FCSTD DOCUMENT  (FreeCAD 0.15R4671 (Git))
Label: BottomCorner
License: All rights reserved
LicenseURL: http://en.wikipedia.org/wiki/All_rights_reserved
objects: Sketcher::SketchObject×16, PartDesign::Pocket×15, Part::Feature×6, PartDesign::Fillet×4, Mesh::Feature×3, PartDesign::Chamfer×2, PartDesign::Pad×1
note: 60 computed .brp shape members not serialized (recipe doc carries the construction recipe); baked Part::Feature solids carry a one-line shape summary decoded from their .brp

FEATURE [Mesh::Feature] tempTopCornerCap
FEATURE [Part::Feature] Part__Feature  label="OB1515_45mm001"
  Placement = pos=(0,-20.5,15.5) rot=(1,0,0;1.5708rad)
  shape: bbox 15 x 45 x 15 mm, 158 faces (baked)
FEATURE [Part::Feature] Part__Feature001  label="OB1515_45mm002"
  Placement = pos=(20.5,0,15.5) rot=(0.57735,0.57735,0.57735;2.0944rad)
  shape: bbox 45 x 15 x 15 mm, 158 faces (baked)
FEATURE [Part::Feature] Part__Feature002  label="OB1515_45mm"
  Placement = pos=(7,-7,1) rot=(0,0,1;0.785398rad)
  shape: bbox 21.01 x 21.01 x 45 mm, 158 faces (baked)
FEATURE [Sketcher::SketchObject] Sketch
  Placement = pos=(0,0,8) rot=(0,0,1;0rad)
  sketch-geometry (9):
    g0: LineSegment StartX=-7.5 StartY=7.5 StartZ=0 EndX=65.5 EndY=7.5 EndZ=0
    g1: LineSegment StartX=65.5 StartY=7.5 StartZ=0 EndX=65.5 EndY=-14.5 EndZ=0
    g2: LineSegment StartX=65.5 StartY=-14.5 StartZ=0 EndX=14.5 EndY=-65.5 EndZ=0
    g3: LineSegment StartX=14.5 StartY=-65.5 StartZ=0 EndX=-7.5 EndY=-65.5 EndZ=0
    g4: LineSegment StartX=-7.5 StartY=-65.5 StartZ=0 EndX=-7.5 EndY=7.5 EndZ=0
    g5: LineSegment StartX=7 StartY=4 StartZ=0 EndX=18 EndY=-7 EndZ=0
    g6: LineSegment StartX=18 StartY=-7 StartZ=0 EndX=7 EndY=-18 EndZ=0
    g7: LineSegment StartX=7 StartY=-18 StartZ=0 EndX=-4 EndY=-7 EndZ=0
    g8: LineSegment StartX=-4 StartY=-7 StartZ=0 EndX=7 EndY=4 EndZ=0
  constraints (18):
    c: Coincident(g0,g1)
    c: Coincident(g1,g2)
    c: Coincident(g2,g3)
    c: Coincident(g3,g4)
    c: Coincident(g4,g0)
    c: Horizontal(g3)
    c: Horizontal(g0)
    c: Vertical(g1)
    c: Vertical(g4)
    c: Angle(g2,g-2) = 0.785398
    c: DistanceX(g0) = -7.5
    c: DistanceY(g0) = 7.5
    c: Coincident(g5,g6)
    c: Coincident(g6,g7)
    c: Coincident(g7,g8)
    c: Coincident(g8,g5)
    c: DistanceY(g3) = -65.5
    c: DistanceX(g0) = 65.5
FEATURE [PartDesign::Pad] Pad
  Length = 88
  Length2 = 100
  Placement = pos=(0,0,8) rot=(0,0,1;0rad)
  Sketch = -> Sketch
  Type = 0
FEATURE [Part::Feature] Part__Feature003  label="OB1515_45mm003"
  Placement = pos=(0,-20.5,88.5) rot=(1,0,0;1.5708rad)
  shape: bbox 15 x 45 x 15 mm, 158 faces (baked)
FEATURE [Part::Feature] Part__Feature004  label="OB1515_45mm004"
  Placement = pos=(20.5,0,88.5) rot=(0.57735,0.57735,0.57735;2.0944rad)
  shape: bbox 45 x 15 x 15 mm, 158 faces (baked)
FEATURE [Sketcher::SketchObject] Sketch001
  Placement = pos=(0,0,96) rot=(0,0,1;0rad)
  Support = -> Pad [Face11]
  sketch-geometry (8):
    g0: LineSegment StartX=20.5 StartY=8.5 StartZ=0 EndX=66.5 EndY=8.5 EndZ=0
    g1: LineSegment StartX=66.5 StartY=8.5 StartZ=0 EndX=66.5 EndY=-7.5 EndZ=0
    g2: LineSegment StartX=66.5 StartY=-7.5 StartZ=0 EndX=20.5 EndY=-7.5 EndZ=0
    g3: LineSegment StartX=20.5 StartY=-7.5 StartZ=0 EndX=20.5 EndY=8.5 EndZ=0
    g4: LineSegment StartX=-8.5 StartY=-20.5 StartZ=0 EndX=7.5 EndY=-20.5 EndZ=0
    g5: LineSegment StartX=7.5 StartY=-20.5 StartZ=0 EndX=7.5 EndY=-66 EndZ=0
    g6: LineSegment StartX=7.5 StartY=-66 StartZ=0 EndX=-8.5 EndY=-66 EndZ=0
    g7: LineSegment StartX=-8.5 StartY=-66 StartZ=0 EndX=-8.5 EndY=-20.5 EndZ=0
  constraints (16):
    c: Coincident(g0,g1)
    c: Coincident(g1,g2)
    c: Coincident(g2,g3)
    c: Coincident(g3,g0)
    c: Horizontal(g0)
    c: Horizontal(g2)
    c: Vertical(g1)
    c: Vertical(g3)
    c: Coincident(g4,g5)
    c: Coincident(g5,g6)
    c: Coincident(g6,g7)
    c: Coincident(g7,g4)
    c: Horizontal(g4)
    c: Horizontal(g6)
    c: Vertical(g5)
    c: Vertical(g7)
FEATURE [PartDesign::Pocket] Pocket
  Length = 5
  Placement = pos=(0,0,8) rot=(0,0,1;0rad)
  Sketch = -> Sketch001
  Type = 1
FEATURE [Sketcher::SketchObject] Sketch002
  Placement = pos=(0,0,96) rot=(0,0,1;0rad)
  Support = -> Pocket [Face4]
  sketch-geometry (4):
    g0: LineSegment StartX=66.5 StartY=-14.5 StartZ=0 EndX=20.5 EndY=-14.5 EndZ=0
    g1: LineSegment StartX=20.5 StartY=-14.5 StartZ=0 EndX=14.5 EndY=-20.5 EndZ=0
    g2: LineSegment StartX=14.5 StartY=-20.5 StartZ=0 EndX=14.5 EndY=-66.5 EndZ=0
    g3: LineSegment StartX=14.5 StartY=-66.5 StartZ=0 EndX=66.5 EndY=-14.5 EndZ=0
  constraints (4):
    c: Coincident(g0,g1)
    c: Coincident(g1,g2)
    c: Coincident(g2,g3)
    c: Coincident(g3,g0)
FEATURE [PartDesign::Pocket] Pocket001
  Length = 81
  Placement = pos=(0,0,8) rot=(0,0,1;0rad)
  Sketch = -> Sketch002
  Type = 0
FEATURE [Sketcher::SketchObject] Sketch003
  Placement = pos=(17.5,-17.5,8) rot=(0.862856,0.357407,0.357407;1.71777rad)
  Support = -> Pocket001 [Face17]
  sketch-geometry (4):
    g0: ArcOfCircle CenterX=0 CenterY=12 CenterZ=0 NormalX=0 NormalY=0 NormalZ=1 Radius=1.52224 StartAngle=3.14159 EndAngle=6.28319
    g1: ArcOfCircle CenterX=0 CenterY=83 CenterZ=0 NormalX=0 NormalY=0 NormalZ=1 Radius=1.52224 StartAngle=0 EndAngle=3.14159
    g2: LineSegment StartX=1.52224 StartY=12 StartZ=0 EndX=1.52224 EndY=83 EndZ=0
    g3: LineSegment StartX=-1.52224 StartY=12 StartZ=0 EndX=-1.52224 EndY=83 EndZ=0
  constraints (6):
    c: Tangent(g0,g3) = 1.5708
    c: Tangent(g0,g2) = -1.5708
    c: Tangent(g2,g1) = -1.5708
    c: Tangent(g3,g1) = 1.5708
    c: Vertical(g2)
    c: Equal(g0,g1)
FEATURE [PartDesign::Pocket] Pocket002
  Length = 15
  Placement = pos=(0,0,8) rot=(0,0,1;0rad)
  Sketch = -> Sketch003
  Type = 0
FEATURE [PartDesign::Chamfer] Chamfer
  Base = -> Pocket002 [Edge4]
  Placement = pos=(0,0,8) rot=(0,0,1;0rad)
  Size = 8
FEATURE [PartDesign::Fillet] Fillet
  Base = -> Chamfer [Edge2,Edge18]
  Placement = pos=(0,0,8) rot=(0,0,1;0rad)
  Radius = 4
FEATURE [Sketcher::SketchObject] Sketch004
  Placement = pos=(0,0,15) rot=(0,0,1;0rad)
  Support = -> Fillet [Face22]
  sketch-geometry (1):
    g0: Circle CenterX=30 CenterY=-30 CenterZ=0 NormalX=0 NormalY=0 NormalZ=1 Radius=2.75
  constraints (1):
    c: Radius(g0) = 2.75
FEATURE [PartDesign::Pocket] Pocket003
  Length = 5
  Placement = pos=(0,0,8) rot=(0,0,1;0rad)
  Sketch = -> Sketch004
  Type = 1
FEATURE [Sketcher::SketchObject] Sketch005
  Placement = pos=(0,-14.5,8) rot=(1,0,0;1.5708rad)
  Support = -> Pocket003 [Face20]
  sketch-geometry (4):
    g0: Circle CenterX=60 CenterY=7.5 CenterZ=0 NormalX=0 NormalY=0 NormalZ=1 Radius=1.8
    g1: Circle CenterX=25 CenterY=7.5 CenterZ=0 NormalX=0 NormalY=0 NormalZ=1 Radius=1.8
    g2: Circle CenterX=25 CenterY=80.5 CenterZ=0 NormalX=0 NormalY=0 NormalZ=1 Radius=1.8
    g3: Circle CenterX=60 CenterY=80.5 CenterZ=0 NormalX=0 NormalY=0 NormalZ=1 Radius=1.8
  constraints (4):
    c: Radius(g2) = 1.8
    c: Radius(g3) = 1.8
    c: Radius(g0) = 1.8
    c: Radius(g1) = 1.8
FEATURE [PartDesign::Pocket] Pocket004
  Length = 5
  Placement = pos=(0,0,8) rot=(0,0,1;0rad)
  Sketch = -> Sketch005
  Type = 1
FEATURE [Sketcher::SketchObject] Sketch006
  Placement = pos=(14.5,0,8) rot=(0.57735,0.57735,0.57735;2.0944rad)
  Support = -> Pocket004 [Face22]
  sketch-geometry (4):
    g0: Circle CenterX=-60 CenterY=7.5 CenterZ=0 NormalX=0 NormalY=0 NormalZ=1 Radius=1.8
    g1: Circle CenterX=-25 CenterY=7.5 CenterZ=0 NormalX=0 NormalY=0 NormalZ=1 Radius=1.8
    g2: Circle CenterX=-60 CenterY=80.5 CenterZ=0 NormalX=0 NormalY=0 NormalZ=1 Radius=1.8
    g3: Circle CenterX=-25 CenterY=80.5 CenterZ=0 NormalX=0 NormalY=0 NormalZ=1 Radius=1.8
  constraints (4):
    c: Radius(g2) = 1.8
    c: Radius(g3) = 1.8
    c: Radius(g1) = 1.8
    c: Radius(g0) = 1.8
FEATURE [PartDesign::Pocket] Pocket005
  Length = 5
  Placement = pos=(0,0,8) rot=(0,0,1;0rad)
  Sketch = -> Sketch006
  Type = 1
FEATURE [PartDesign::Fillet] Fillet001
  Base = -> Pocket005 [Edge80,Edge69]
  Placement = pos=(0,0,8) rot=(0,0,1;0rad)
  Radius = 4
FEATURE [Sketcher::SketchObject] Sketch007
  Placement = pos=(14.5,0,8) rot=(0.57735,0.57735,0.57735;2.0944rad)
  Support = -> Fillet001 [Face9]
  sketch-geometry (4):
    g0: Circle CenterX=-60 CenterY=80.5 CenterZ=0 NormalX=0 NormalY=0 NormalZ=1 Radius=3.6
    g1: Circle CenterX=-25 CenterY=80.5 CenterZ=0 NormalX=0 NormalY=0 NormalZ=1 Radius=3.6
    g2: Circle CenterX=-60 CenterY=7.5 CenterZ=0 NormalX=0 NormalY=0 NormalZ=1 Radius=3.6
    g3: Circle CenterX=-25 CenterY=7.5 CenterZ=0 NormalX=0 NormalY=0 NormalZ=1 Radius=3.6
  constraints (4):
    c: Radius(g0) = 3.6
    c: Radius(g1) = 3.6
    c: Radius(g2) = 3.6
    c: Radius(g3) = 3.6
FEATURE [PartDesign::Pocket] Pocket006
  Length = 6
  Midplane = true
  Placement = pos=(0,0,8) rot=(0,0,1;0rad)
  Sketch = -> Sketch007
  Type = 0
FEATURE [Sketcher::SketchObject] Sketch008
  Placement = pos=(0,-14.5,8) rot=(1,0,0;1.5708rad)
  Support = -> Pocket006 [Face2]
  sketch-geometry (4):
    g0: Circle CenterX=60 CenterY=7.5 CenterZ=0 NormalX=0 NormalY=0 NormalZ=1 Radius=3.6
    g1: Circle CenterX=25 CenterY=7.5 CenterZ=0 NormalX=0 NormalY=0 NormalZ=1 Radius=3.6
    g2: Circle CenterX=25 CenterY=80.5 CenterZ=0 NormalX=0 NormalY=0 NormalZ=1 Radius=3.6
    g3: Circle CenterX=60 CenterY=80.5 CenterZ=0 NormalX=0 NormalY=0 NormalZ=1 Radius=3.6
  constraints (4):
    c: Radius(g2) = 3.6
    c: Radius(g3) = 3.6
    c: Radius(g1) = 3.6
    c: Radius(g0) = 3.6
FEATURE [PartDesign::Pocket] Pocket007
  Length = 6
  Midplane = true
  Placement = pos=(0,0,8) rot=(0,0,1;0rad)
  Sketch = -> Sketch008
  Type = 0
FEATURE [Sketcher::SketchObject] Sketch009
  Placement = pos=(0,0,15) rot=(0,0,1;0rad)
  Support = -> Pocket007 [Face24]
  sketch-geometry (8):
    g0: LineSegment StartX=56 StartY=-14.5 StartZ=0 EndX=65.5 EndY=-14.5 EndZ=0
    g1: LineSegment StartX=65.5 StartY=-14.5 StartZ=0 EndX=65.5 EndY=-24.5 EndZ=0
    g2: LineSegment StartX=65.5 StartY=-24.5 StartZ=0 EndX=56 EndY=-24.5 EndZ=0
    g3: LineSegment StartX=56 StartY=-24.5 StartZ=0 EndX=56 EndY=-14.5 EndZ=0
    g4: LineSegment StartX=14.5 StartY=-56 StartZ=0 EndX=29.7351 EndY=-56 EndZ=0
    g5: LineSegment StartX=29.7351 StartY=-56 StartZ=0 EndX=29.7351 EndY=-66 EndZ=0
    g6: LineSegment StartX=29.7351 StartY=-66 StartZ=0 EndX=14.5 EndY=-66 EndZ=0
    g7: LineSegment StartX=14.5 StartY=-66 StartZ=0 EndX=14.5 EndY=-56 EndZ=0
  constraints (16):
    c: Coincident(g0,g1)
    c: Coincident(g1,g2)
    c: Coincident(g2,g3)
    c: Coincident(g3,g0)
    c: Horizontal(g0)
    c: Horizontal(g2)
    c: Vertical(g1)
    c: Vertical(g3)
    c: Coincident(g4,g5)
    c: Coincident(g5,g6)
    c: Coincident(g6,g7)
    c: Coincident(g7,g4)
    c: Horizontal(g4)
    c: Horizontal(g6)
    c: Vertical(g5)
    c: Vertical(g7)
FEATURE [PartDesign::Pocket] Pocket008
  Length = 5
  Placement = pos=(0,0,8) rot=(0,0,1;0rad)
  Sketch = -> Sketch009
  Type = 1
FEATURE [PartDesign::Fillet] Fillet002
  Base = -> Pocket008 [Edge165,Edge164]
  Placement = pos=(0,0,8) rot=(0,0,1;0rad)
  Radius = 4
FEATURE [Sketcher::SketchObject] Sketch010
  Placement = pos=(0,-65.5,8) rot=(1,0,0;1.5708rad)
  Support = -> Fillet002 [Face20]
  sketch-geometry (6):
    g0: LineSegment StartX=15.5 StartY=73 StartZ=0 EndX=14.5 EndY=73 EndZ=0
    g1: LineSegment StartX=14.5 StartY=73 StartZ=0 EndX=11 EndY=69.5 EndZ=0
    g2: LineSegment StartX=11 StartY=69.5 StartZ=0 EndX=11 EndY=18.5 EndZ=0
    g3: LineSegment StartX=11 StartY=18.5 StartZ=0 EndX=14.5 EndY=15 EndZ=0
    g4: LineSegment StartX=14.5 StartY=15 StartZ=0 EndX=15.5 EndY=15 EndZ=0
    g5: LineSegment StartX=15.5 StartY=15 StartZ=0 EndX=15.5 EndY=73 EndZ=0
  constraints (6):
    c: Coincident(g0,g1)
    c: Coincident(g1,g2)
    c: Coincident(g2,g3)
    c: Coincident(g3,g4)
    c: Coincident(g4,g5)
    c: Coincident(g5,g0)
FEATURE [PartDesign::Pocket] Pocket009
  Length = 38
  Placement = pos=(0,0,8) rot=(0,0,1;0rad)
  Sketch = -> Sketch010
  Type = 0
FEATURE [Sketcher::SketchObject] Sketch011
  Placement = pos=(65.5,0,8) rot=(0.57735,0.57735,0.57735;2.0944rad)
  Support = -> Pocket009 [Face30]
  sketch-geometry (6):
    g0: LineSegment StartX=-15.5 StartY=73 StartZ=0 EndX=-14.5 EndY=73 EndZ=0
    g1: LineSegment StartX=-14.5 StartY=73 StartZ=0 EndX=-11 EndY=69.5 EndZ=0
    g2: LineSegment StartX=-11 StartY=69.5 StartZ=0 EndX=-11 EndY=18.5 EndZ=0
    g3: LineSegment StartX=-11 StartY=18.5 StartZ=0 EndX=-14.5 EndY=15 EndZ=0
    g4: LineSegment StartX=-14.5 StartY=15 StartZ=0 EndX=-15.5 EndY=15 EndZ=0
    g5: LineSegment StartX=-15.5 StartY=15 StartZ=0 EndX=-15.5 EndY=73 EndZ=0
  constraints (6):
    c: Coincident(g0,g1)
    c: Coincident(g1,g2)
    c: Coincident(g2,g3)
    c: Coincident(g3,g4)
    c: Coincident(g4,g5)
    c: Coincident(g5,g0)
FEATURE [PartDesign::Pocket] Pocket010
  Length = 38
  Placement = pos=(0,0,8) rot=(0,0,1;0rad)
  Sketch = -> Sketch011
  Type = 0
FEATURE [PartDesign::Chamfer] Chamfer001
  Base = -> Pocket010 [Edge26,Edge62]
  Placement = pos=(0,0,8) rot=(0,0,1;0rad)
  Size = 3.499
FEATURE [Sketcher::SketchObject] Sketch012
  Placement = pos=(-3.5,3.5,8) rot=(-0.281085,0.678598,0.678598;3.68962rad)
  Support = -> Chamfer001 [Face26]
  sketch-geometry (2):
    g0: Circle CenterX=0 CenterY=7.5 CenterZ=0 NormalX=0 NormalY=0 NormalZ=1 Radius=1.8
    g1: Circle CenterX=0 CenterY=80.5 CenterZ=0 NormalX=0 NormalY=0 NormalZ=1 Radius=1.8
  constraints (2):
    c: Radius(g1) = 1.8
    c: Radius(g0) = 1.8
FEATURE [PartDesign::Pocket] Pocket011
  Length = 15
  Placement = pos=(0,0,8) rot=(0,0,1;0rad)
  Sketch = -> Sketch012
  Type = 0
FEATURE [Sketcher::SketchObject] Sketch013
  Placement = pos=(-3.5,3.5,8) rot=(-0.281085,0.678598,0.678598;3.68962rad)
  Support = -> Pocket011 [Face26]
  sketch-geometry (2):
    g0: Circle CenterX=0 CenterY=80.5 CenterZ=0 NormalX=0 NormalY=0 NormalZ=1 Radius=3.6
    g1: Circle CenterX=0 CenterY=7.5 CenterZ=0 NormalX=0 NormalY=0 NormalZ=1 Radius=3.6
  constraints (2):
    c: Radius(g1) = 3.6
    c: Radius(g0) = 3.6
FEATURE [PartDesign::Pocket] Pocket012
  Length = 3
  Placement = pos=(0,0,8) rot=(0,0,1;0rad)
  Sketch = -> Sketch013
  Type = 0
FEATURE [Mesh::Feature] GEMINI_R  label="GEMINI R5"
FEATURE [Part::Feature] Pocket013  label="BottomCorner_1"
  shape: bbox 73 x 73 x 88 mm, 75 faces (baked)
FEATURE [Sketcher::SketchObject] Sketch014
  Placement = pos=(0,-65.5,0) rot=(1,0,0;1.5708rad)
  Support = -> Pocket013 [Face13]
  sketch-geometry (4):
    g0: LineSegment StartX=-10.5 StartY=98 StartZ=0 EndX=66.5 EndY=98 EndZ=0
    g1: LineSegment StartX=66.5 StartY=98 StartZ=0 EndX=66.5 EndY=23 EndZ=0
    g2: LineSegment StartX=66.5 StartY=23 StartZ=0 EndX=-10.5 EndY=23 EndZ=0
    g3: LineSegment StartX=-10.5 StartY=23 StartZ=0 EndX=-10.5 EndY=98 EndZ=0
  constraints (8):
    c: Coincident(g0,g1)
    c: Coincident(g1,g2)
    c: Coincident(g2,g3)
    c: Coincident(g3,g0)
    c: Horizontal(g0)
    c: Horizontal(g2)
    c: Vertical(g1)
    c: Vertical(g3)
FEATURE [PartDesign::Pocket] Pocket014  label="BottomShortCorner_1"
  Length = 5
  Sketch = -> Sketch014
  Type = 1
FEATURE [PartDesign::Fillet] Fillet003  label="BottomShortCorner"
  Base = -> Pocket014 [Edge28,Edge34]
  Radius = 2
FEATURE [Mesh::Feature] TopCornerIdler_II
FEATURE [Sketcher::SketchObject] Sketch015
  Placement = pos=(0,0,96) rot=(0,0,1;0rad)
  Support = -> Pocket013 [Face15]
  sketch-geometry (8):
    g0: LineSegment StartX=-0.75 StartY=-20 StartZ=0 EndX=0.75 EndY=-20 EndZ=0
    g1: LineSegment StartX=0.75 StartY=-20 StartZ=0 EndX=0.75 EndY=-21.25 EndZ=0
    g2: LineSegment StartX=0.75 StartY=-21.25 StartZ=0 EndX=-0.75 EndY=-21.25 EndZ=0
    g3: LineSegment StartX=-0.75 StartY=-21.25 StartZ=0 EndX=-0.75 EndY=-20 EndZ=0
    g4: LineSegment StartX=20 StartY=0.75 StartZ=0 EndX=23 EndY=0.75 EndZ=0
    g5: LineSegment StartX=23 StartY=0.75 StartZ=0 EndX=23 EndY=-0.75 EndZ=0
    g6: LineSegment StartX=23 StartY=-0.75 StartZ=0 EndX=20 EndY=-0.75 EndZ=0
    g7: LineSegment StartX=20 StartY=-0.75 StartZ=0 EndX=20 EndY=0.75 EndZ=0
  constraints (16):
    c: Coincident(g0,g1)
    c: Coincident(g1,g2)
    c: Coincident(g2,g3)
    c: Coincident(g3,g0)
    c: Horizontal(g0)
    c: Horizontal(g2)
    c: Vertical(g1)
    c: Vertical(g3)
    c: Coincident(g4,g5)
    c: Coincident(g5,g6)
    c: Coincident(g6,g7)
    c: Coincident(g7,g4)
    c: Horizontal(g4)
    c: Horizontal(g6)
    c: Vertical(g5)
    c: Vertical(g7)
FEATURE [PartDesign::Pocket] Pocket015  label="BottomCorner_Tall"
  Length = 5
  Sketch = -> Sketch015
  Type = 1
